# Revit family: STH20250_27
name_source: partatom
category: Luminárias
units: mm (PartAtom-declared; Revit-internal decimal feet)

## family parameters
Com base no plano de trabalho = Não
Compartilhado = Não
Corte com vazios quando carregada = Não
Cota do conector redondo = Utilizar diâmetro
Fonte luminosa = Sim
Manter orientação da anotação = Não
Ponto de cálculo do ambiente = Não
Sempre na vertical = Sim
Tipo de parte = Normal

## types (1)
- STH20250/27 - BIVOLT - 2700K - 810lm - 220°
    Altura = 0.12 m
    Arquivo de rede fotométrica = STELLA - STH20250-27 - BULBO 9,8W DIM.ies
    Dimerização = 20-100%
    Diâmetro = 0.06 m
    Elevação padrão = 0 m
    Estrutura = Al - Branco
    Fabricante = Stella
    Filtro de cor = 16777215
    Fluxo Luminoso = 810 lm
    Grau de proteção (IP) = IP20
    IRC (Índice de reprodução de cores) = >80
    Luminoso = Luminoso - 2700K
    Modelo = Bulbo DIM
    Potência = 10 W
    Referência = STH20250/27 - BIVOLT
    Temperatura da cor (K) = 2700 K
    Tensão Elétrica = 100V-240V
    Troca de temperatura da cor de lâmpada com esmaecimento = <Nenhum>
    URL = https://stella.com.br
    Ângulo de Abertura = 220º
    Ângulo de inclinação = 90.00°
